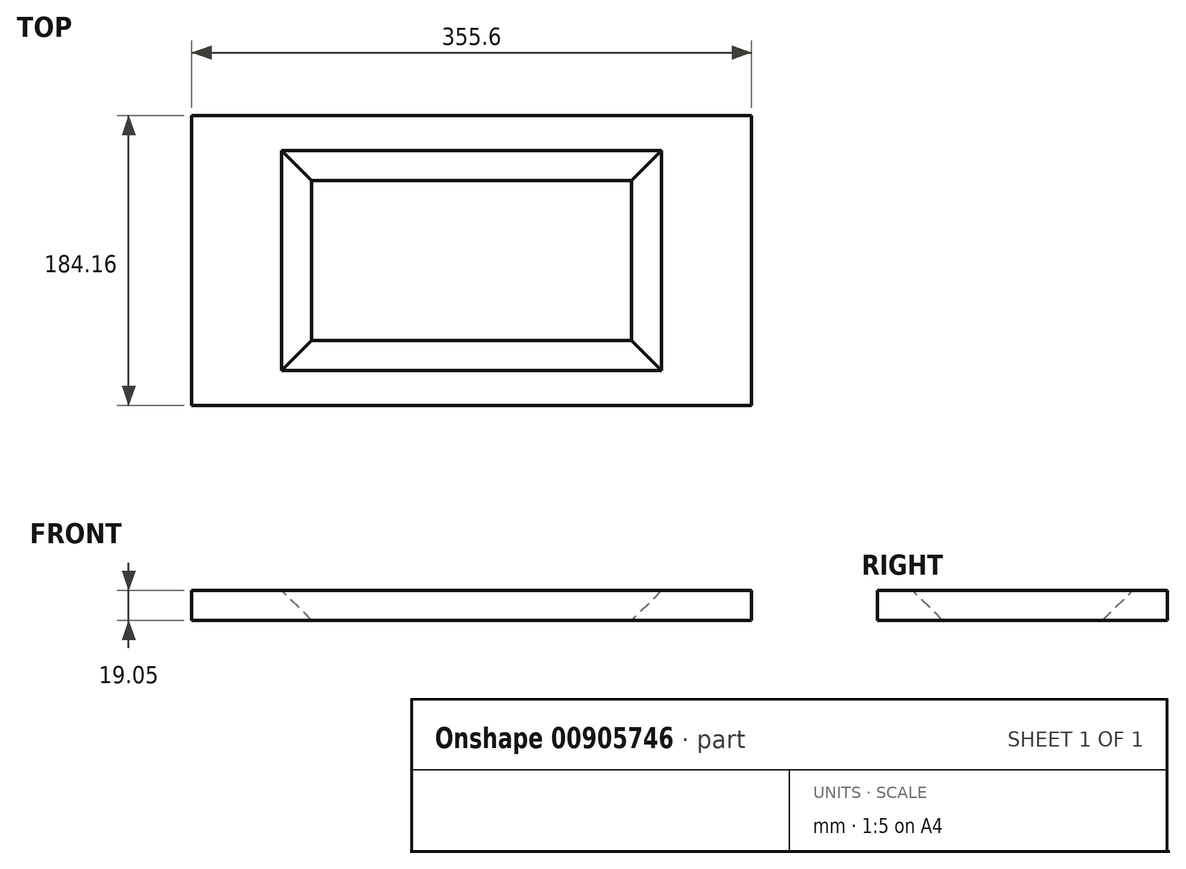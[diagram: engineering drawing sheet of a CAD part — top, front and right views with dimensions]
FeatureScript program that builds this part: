
annotation { "Feature Type Name" : "Feature", "Feature Type Description" : "" }
export const myFeature = defineFeature(function(context is Context, id is Id, definition is map)
    precondition{}
    {
        {
            var Q0;
            Q0=qCreatedBy(makeId("Top.planeOp"),FACE);
            var sketch = newSketch(context, id + "F0", { "sketchPlane" : qUnion([Q0])});
            skLineSegment(sketch, "E0.bottom", {"start": v(177.8, 92.08) * mm, "end": v(-177.8, 92.08) * mm});
            skLineSegment(sketch, "E0.top", {"start": v(177.8, -92.08) * mm, "end": v(-177.8, -92.08) * mm});
            skLineSegment(sketch, "E0.left", {"start": v(177.8, 92.08) * mm, "end": v(177.8, -92.08) * mm});
            skLineSegment(sketch, "E0.right", {"start": v(-177.8, 92.08) * mm, "end": v(-177.8, -92.08) * mm});
            skPoint(sketch, "E0.middle", {"position": v(0, 0) * mm});
            skLineSegment(sketch, "E1.bottom", {"start": v(101.6, 50.8) * mm, "end": v(-101.6, 50.8) * mm});
            skLineSegment(sketch, "E1.top", {"start": v(101.6, -50.8) * mm, "end": v(-101.6, -50.8) * mm});
            skLineSegment(sketch, "E1.left", {"start": v(101.6, 50.8) * mm, "end": v(101.6, -50.8) * mm});
            skLineSegment(sketch, "E1.right", {"start": v(-101.6, 50.8) * mm, "end": v(-101.6, -50.8) * mm});
            skSolve(sketch);
        }
        {
            var Q0;
            Q0 = qSketchRegion(id + "F0", true);
            extrude(context, id + "F1", {"entities" : qUnion([Q0]), "depth" : 19.05 * mm, "offsetDistance" : 25.4 * mm});
        }
        {
            var Q0;
            Q0=makeQuery(id+"F1.opExtrude","CAP_EDGE",EDGE,{"disambiguationData":[OSD([sQuery(id+"F0.wireOp",EDGE,"E1.right")])],"isStart":false});
            var Q1;
            Q1=makeQuery(id+"F1.opExtrude","CAP_EDGE",EDGE,{"disambiguationData":[OSD([sQuery(id+"F0.wireOp",EDGE,"E1.bottom")])],"isStart":false});
            var Q2;
            Q2=makeQuery(id+"F1.opExtrude","CAP_EDGE",EDGE,{"disambiguationData":[OSD([sQuery(id+"F0.wireOp",EDGE,"E1.left")])],"isStart":false});
            var Q3;
            Q3=makeQuery(id+"F1.opExtrude","CAP_EDGE",EDGE,{"disambiguationData":[OSD([sQuery(id+"F0.wireOp",EDGE,"E1.top")])],"isStart":false});
            chamfer(context, id + "F2", {"entities" : qUnion([Q0, Q1, Q2, Q3]), "chamferType" : ChamferType.OFFSET_ANGLE, "width" : 19.05 * mm, "oppositeDirection" : false, "angle" : 45 * degree, "tangentPropagation" : true});
        }
    });
